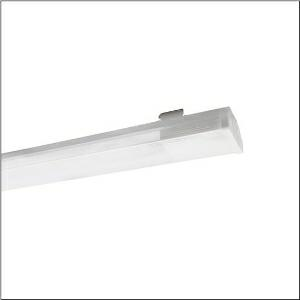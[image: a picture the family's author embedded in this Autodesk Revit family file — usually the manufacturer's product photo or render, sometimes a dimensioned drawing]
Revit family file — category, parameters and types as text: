
# Revit family: modario_31_gen_2_53bm8117u4l3d2_6779
name_source: partatom
category: Lighting Fixtures
units: mm (PartAtom-declared; Revit-internal decimal feet)

## family parameters
Cut with Voids When Loaded = No
Host = Face
Light Source = No
Part Type = Normal
Room Calculation Point = No
Round Connector Dimension = Use Diameter
Shared = No

## types (1)
- Modario 31 Gen.2 (1 x LED, 23600 lm, 126 W, 4000K)
    Apparent Load = 126 VA
    CIE Flux Codes = 50 78 94 90 100
    Color Rendering = 80
    Color Temperature = 4000K
    Default Elevation = 1800 mm
    Description = Modario 31 Gen.2, luminaire insert, of sheet steel, coil coated, white, length: 2.392mm, width: 81mm, height: 82mm, 8x system unit, system units: 299mm, LED rated luminous flux: 23.600lm, light colour: 840, SDCM (Standard Deviation of Colour Matching)MacAdam ≤ 3 SDCM (initial), control gear: ON/OFF, with plug, 3-pole, with phase selection, mains connection: 220..240V, AC, 50/60Hz, rated input power: 126W, through-wiring accessed according to module size, primary optical cover: cover, of PMMA, light emission: direct distribution, primary light characteristic: symmetric, protection rating (complete): IP20, protection rating (LED compartment): IP50, insulation class (complete): insulation class I (protective earthing), certification: CE, ENEC, VDE, UKCA, impact resistance: IK03, permissible ambient temperature for indoor applications: -40..+35°C, corresponds to IFS (International Featured Standards) requirements for safety and quality in the food industry, reducing of maximum allowable ambient temperature of 5°C with ceiling mounting, IP40 when using the optional accessory 5TP9018, packaging unit: 1 piece
    Height = 92 mm
    Lamp = 1 x LED
    Lamp Light Flux = 23600 lm
    Lamp Power = 126 W
    Lamp count = 1
    Length = 2392 mm
    Luminous efficacy = 187 lm/W
    Manufacturer = Siteco
    ModVariant = No
    Model = 53BM8117U4L3D2
    Mounting Place = Ceiling
    Mounting Type = Pendant
    Number of Poles = 1
    OnlyDefault = Yes
    Power Factor = 1
    Product Name = Modario 31 Gen.2
    Product group = luminaire insert | ceiling pendant
    ProductGroupID = 901
    Protection Class = Protection class I
    Protection Degree = IP 20
    RLX_Detail_Level = 1
    RLX_Emergency_Light_Flux = 0 lm
    RLX_Emergency_Type = 0
    RLX_Emergency_Type_DB = No
    RlxData = <blob elided: 34861 chars, md5=a161d8a9>
    Socket = socket
    Standby Power = 0 W
    System Light Flux = 23600 lm
    System Power = 126 W
    Type Comments = Product without accessories
    Type Image = l_1341883.jpg
    URL = http://relux.com
    VarID = ---
    Voltage = 0 V
    Weight = 0.00 kg
    Width = 81 mm

## geometry (parser evidence)
native form markers: Blend x4, Sweep x14
no freeform markers — native parametric forms only
